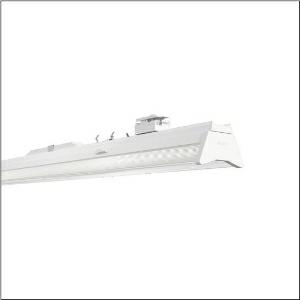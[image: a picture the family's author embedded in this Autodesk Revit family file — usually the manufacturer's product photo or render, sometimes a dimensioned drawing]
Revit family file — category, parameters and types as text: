
# Revit family: licross_21_performance_mo_52tm16dn4a5g
name_source: partatom
category: Lighting Fixtures
units: mm (PartAtom-declared; Revit-internal decimal feet)

## family parameters
Cut with Voids When Loaded = No
Host = Face
Light Source = No
Part Type = Normal
Room Calculation Point = No
Round Connector Dimension = Use Diameter
Shared = No

## types (1)
- --- (1 x LED, 10840 lm, 62 W, 4000K)
    Apparent Load = 62 VA
    CIE Flux Codes = 66 88 96 79 100
    Color Rendering = 80
    Color Temperature = 4000K
    Default Elevation = 1800 mm
    Description = Licross 21 Performance MO, luminaire insert, of sheet steel, galvanised, coil coated, white, length: 1.500mm, width: 120mm, height: 123mm, LED rated luminous flux: 10.840lm, light colour: 840, SDCM (Standard Deviation of Colour Matching)MacAdam ≤ 3 SDCM (initial), control gear: DALI 2, with plug, 5-pole, with phase selection, mains connection: 220..240V, AC, 50/60Hz, rated input power: 62W, internal wiring halogen-free, primary light control with lens, of plastic, primary optical cover: cover, of PMMA, light emission: direct/indirect distribution, primary light characteristic: symmetric, protection rating (complete): IP40, insulation class (complete): insulation class I (protective earthing), certification: CE, ENEC, UKCA, protection symbol: D if used in an environment without relevant dust loads with corresponding accessories, impact resistance: IK06, permissible ambient temperature for indoor applications: -25..+35°C, corresponds to IFS (International Featured Standards) requirements for safety and quality in the food industry, reducing of maximum allowable ambient temperature of 5°C with ceiling mounting, LABS conformity tested according to VDMA 24364:2018-05, The light source and the operating device comply with the requirements of the Ecodesign Regulation (EU) 2019/2020 and are replaceable in accordance with this regulation, packaging unit: 1 piece
    Height = 114 mm
    Lamp = 1 x LED
    Lamp Light Flux = 10840 lm
    Lamp Power = 62 W
    Lamp count = 1
    Length = 1500 mm
    Luminous efficacy = 175 lm/W
    Manufacturer = Siteco
    ModVariant = No
    Model = 52TM16DN4A5G
    Mounting Place = Ceiling
    Mounting Type = Pendant
    Number of Poles = 1
    OnlyDefault = Yes
    Power Factor = 1
    Product Name = Licross 21 Performance MO
    Product group = luminaire insert | ceiling pendant
    ProductGroupID = 901
    Protection Class = Protection class I
    Protection Degree = IP 40
    RLX_Detail_Level = 1
    RLX_Emergency_Light_Flux = 0 lm
    RLX_Emergency_Type = 0
    RLX_Emergency_Type_DB = No
    RlxData = <blob elided: 34365 chars, md5=779ebb4f>
    Socket = socket
    Standby Power = 0 W
    System Light Flux = 10840 lm
    System Power = 62 W
    Type Comments = factory setting: luminous flux: 100 % | dim-lin: 254 | 418 mA
    Type Image = l_1256138.jpg
    URL = http://relux.com
    VarID = @adj_129393
    Voltage = 0 V
    Weight = 0.00 kg
    Width = 120 mm

## geometry (parser evidence)
native form markers: Blend x4, Sweep x11
no freeform markers — native parametric forms only
